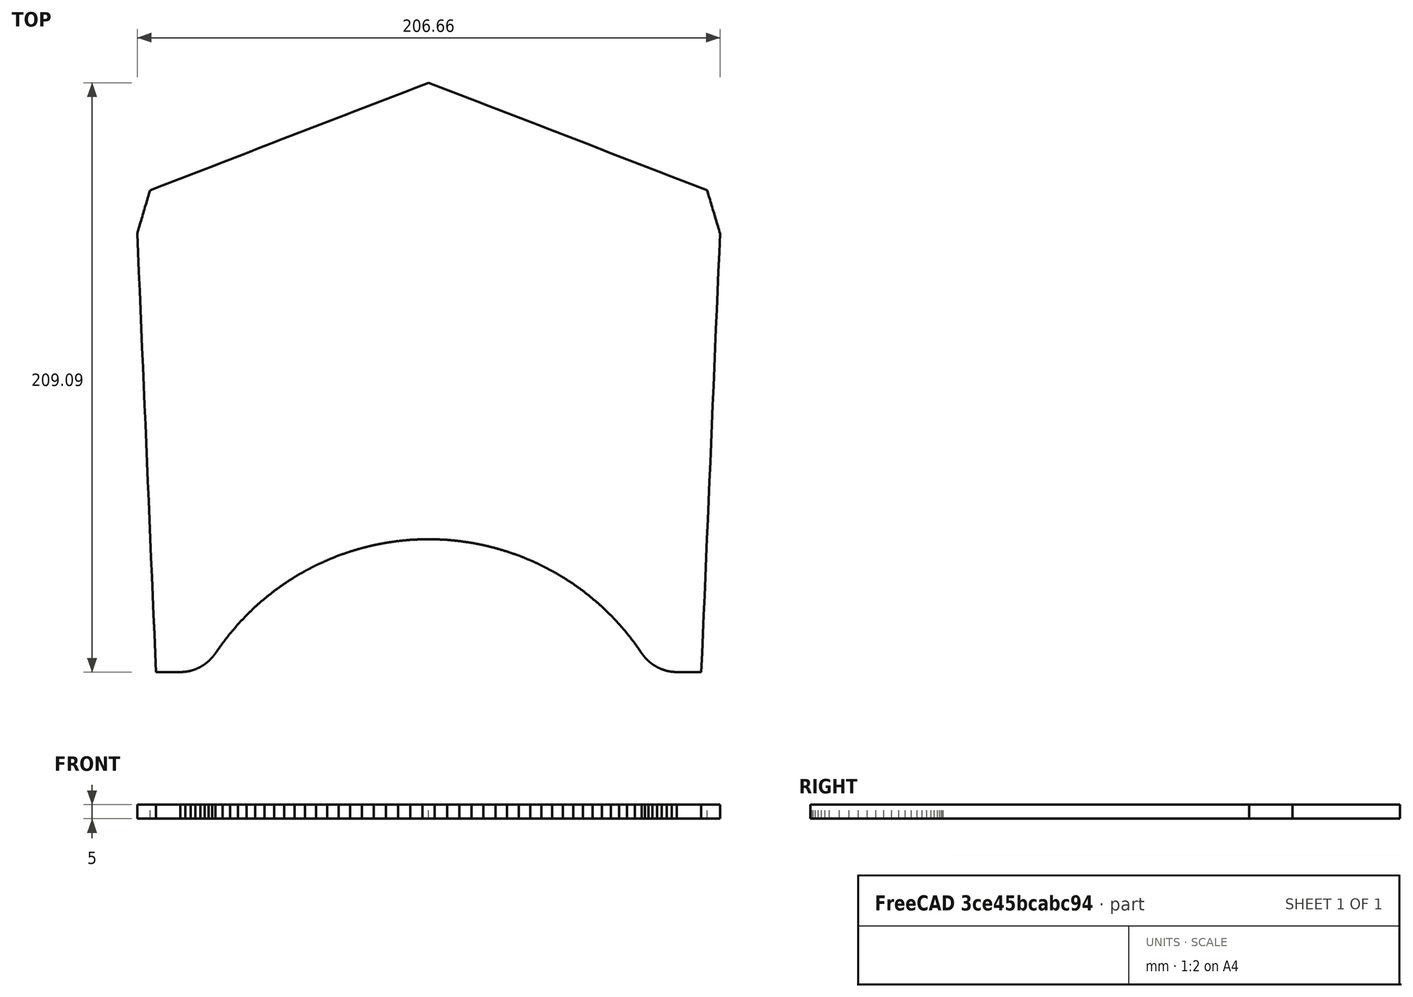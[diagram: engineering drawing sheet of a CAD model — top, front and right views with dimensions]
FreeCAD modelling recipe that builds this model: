
FCSTD DOCUMENT  (FreeCAD 0.19R)
Label: F-35_v2_parts_18
License: All rights reserved
LicenseURL: http://en.wikipedia.org/wiki/All_rights_reserved
objects: App::DocumentObjectGroup×2, PartDesign::CoordinateSystem×2, App::FeaturePython×1, Sketcher::SketchObject×1, PartDesign::Pad×1, PartDesign::Body×1, App::Part×1
note: 6 computed .brp shape members not serialized (recipe doc carries the construction recipe); baked Part::Feature solids carry a one-line shape summary decoded from their .brp

FEATURE [App::DocumentObjectGroup] Parts
FEATURE [PartDesign::CoordinateSystem] LCS_Origin
  AttacherType = Attacher::AttachEngine3D
  MapMode = 2
  Support = -> [X_Axis]
FEATURE [App::DocumentObjectGroup] Constraints
FEATURE [App::FeaturePython] Variables  # WARN: FeaturePython — macro-defined, semantics opaque (R4)
FEATURE [Sketcher::SketchObject] Sketch005
  FullyConstrained = false
  sketch-geometry (65):
    g0: BSplineCurve PolesCount=2 KnotsCount=2 Degree=1 IsPeriodic=0
    g1: BSplineCurve PolesCount=2 KnotsCount=2 Degree=1 IsPeriodic=0
    g2: BSplineCurve PolesCount=2 KnotsCount=2 Degree=1 IsPeriodic=0
    g3: BSplineCurve PolesCount=2 KnotsCount=2 Degree=1 IsPeriodic=0
    g4: BSplineCurve PolesCount=2 KnotsCount=2 Degree=1 IsPeriodic=0
    g5: BSplineCurve PolesCount=2 KnotsCount=2 Degree=1 IsPeriodic=0
    g6: BSplineCurve PolesCount=2 KnotsCount=2 Degree=1 IsPeriodic=0
    g7: BSplineCurve PolesCount=2 KnotsCount=2 Degree=1 IsPeriodic=0
    g8: BSplineCurve PolesCount=2 KnotsCount=2 Degree=1 IsPeriodic=0
    g9: BSplineCurve PolesCount=2 KnotsCount=2 Degree=1 IsPeriodic=0
    g10: BSplineCurve PolesCount=2 KnotsCount=2 Degree=1 IsPeriodic=0
    g11: BSplineCurve PolesCount=2 KnotsCount=2 Degree=1 IsPeriodic=0
    g12: BSplineCurve PolesCount=2 KnotsCount=2 Degree=1 IsPeriodic=0
    g13: BSplineCurve PolesCount=2 KnotsCount=2 Degree=1 IsPeriodic=0
    g14: BSplineCurve PolesCount=2 KnotsCount=2 Degree=1 IsPeriodic=0
    g15: BSplineCurve PolesCount=2 KnotsCount=2 Degree=1 IsPeriodic=0
    g16: BSplineCurve PolesCount=2 KnotsCount=2 Degree=1 IsPeriodic=0
    g17: BSplineCurve PolesCount=2 KnotsCount=2 Degree=1 IsPeriodic=0
    g18: BSplineCurve PolesCount=2 KnotsCount=2 Degree=1 IsPeriodic=0
    g19: BSplineCurve PolesCount=2 KnotsCount=2 Degree=1 IsPeriodic=0
    g20: BSplineCurve PolesCount=2 KnotsCount=2 Degree=1 IsPeriodic=0
    g21: BSplineCurve PolesCount=2 KnotsCount=2 Degree=1 IsPeriodic=0
    g22: BSplineCurve PolesCount=2 KnotsCount=2 Degree=1 IsPeriodic=0
    g23: BSplineCurve PolesCount=2 KnotsCount=2 Degree=1 IsPeriodic=0
    g24: BSplineCurve PolesCount=2 KnotsCount=2 Degree=1 IsPeriodic=0
    g25: BSplineCurve PolesCount=2 KnotsCount=2 Degree=1 IsPeriodic=0
    g26: BSplineCurve PolesCount=2 KnotsCount=2 Degree=1 IsPeriodic=0
    g27: BSplineCurve PolesCount=2 KnotsCount=2 Degree=1 IsPeriodic=0
    g28: BSplineCurve PolesCount=2 KnotsCount=2 Degree=1 IsPeriodic=0
    g29: BSplineCurve PolesCount=2 KnotsCount=2 Degree=1 IsPeriodic=0
    g30: BSplineCurve PolesCount=2 KnotsCount=2 Degree=1 IsPeriodic=0
    g31: BSplineCurve PolesCount=2 KnotsCount=2 Degree=1 IsPeriodic=0
    g32: BSplineCurve PolesCount=2 KnotsCount=2 Degree=1 IsPeriodic=0
    g33: BSplineCurve PolesCount=2 KnotsCount=2 Degree=1 IsPeriodic=0
    g34: BSplineCurve PolesCount=2 KnotsCount=2 Degree=1 IsPeriodic=0
    g35: BSplineCurve PolesCount=2 KnotsCount=2 Degree=1 IsPeriodic=0
    g36: BSplineCurve PolesCount=2 KnotsCount=2 Degree=1 IsPeriodic=0
    g37: BSplineCurve PolesCount=2 KnotsCount=2 Degree=1 IsPeriodic=0
    g38: BSplineCurve PolesCount=2 KnotsCount=2 Degree=1 IsPeriodic=0
    g39: BSplineCurve PolesCount=2 KnotsCount=2 Degree=1 IsPeriodic=0
    g40: BSplineCurve PolesCount=2 KnotsCount=2 Degree=1 IsPeriodic=0
    g41: BSplineCurve PolesCount=2 KnotsCount=2 Degree=1 IsPeriodic=0
    g42: BSplineCurve PolesCount=2 KnotsCount=2 Degree=1 IsPeriodic=0
    g43: BSplineCurve PolesCount=2 KnotsCount=2 Degree=1 IsPeriodic=0
    g44: BSplineCurve PolesCount=2 KnotsCount=2 Degree=1 IsPeriodic=0
    g45: BSplineCurve PolesCount=2 KnotsCount=2 Degree=1 IsPeriodic=0
    g46: BSplineCurve PolesCount=2 KnotsCount=2 Degree=1 IsPeriodic=0
    g47: BSplineCurve PolesCount=2 KnotsCount=2 Degree=1 IsPeriodic=0
    g48: BSplineCurve PolesCount=2 KnotsCount=2 Degree=1 IsPeriodic=0
    g49: BSplineCurve PolesCount=2 KnotsCount=2 Degree=1 IsPeriodic=0
    g50: BSplineCurve PolesCount=2 KnotsCount=2 Degree=1 IsPeriodic=0
    g51: BSplineCurve PolesCount=2 KnotsCount=2 Degree=1 IsPeriodic=0
    g52: BSplineCurve PolesCount=2 KnotsCount=2 Degree=1 IsPeriodic=0
    g53: BSplineCurve PolesCount=2 KnotsCount=2 Degree=1 IsPeriodic=0
    g54: BSplineCurve PolesCount=2 KnotsCount=2 Degree=1 IsPeriodic=0
    g55: BSplineCurve PolesCount=2 KnotsCount=2 Degree=1 IsPeriodic=0
    g56: BSplineCurve PolesCount=2 KnotsCount=2 Degree=1 IsPeriodic=0
    g57: BSplineCurve PolesCount=2 KnotsCount=2 Degree=1 IsPeriodic=0
    g58: BSplineCurve PolesCount=2 KnotsCount=2 Degree=1 IsPeriodic=0
    g59: BSplineCurve PolesCount=2 KnotsCount=2 Degree=1 IsPeriodic=0
    g60: BSplineCurve PolesCount=2 KnotsCount=2 Degree=1 IsPeriodic=0
    g61: BSplineCurve PolesCount=2 KnotsCount=2 Degree=1 IsPeriodic=0
    g62: BSplineCurve PolesCount=2 KnotsCount=2 Degree=1 IsPeriodic=0
    g63: BSplineCurve PolesCount=2 KnotsCount=2 Degree=1 IsPeriodic=0
    g64: BSplineCurve PolesCount=2 KnotsCount=2 Degree=1 IsPeriodic=0
  constraints (54):
    c: Coincident(g0,g1)
    c: Coincident(g1,g2)
    c: Coincident(g2,g3)
    c: Coincident(g3,g4)
    c: Coincident(g4,g5)
    c: Coincident(g5,g6)
    c: Coincident(g6,g7)
    c: Coincident(g9,g10)
    c: Coincident(g10,g11)
    c: Coincident(g11,g12)
    c: Coincident(g12,g13)
    c: Coincident(g13,g14)
    c: Coincident(g14,g15)
    c: Coincident(g15,g16)
    c: Coincident(g16,g17)
    c: Coincident(g17,g18)
    c: Coincident(g18,g19)
    c: Coincident(g19,g20)
    c: Coincident(g20,g21)
    c: Coincident(g21,g22)
    c: Coincident(g22,g23)
    c: Coincident(g23,g24)
    c: Coincident(g24,g25)
    c: Coincident(g25,g26)
    c: Coincident(g26,g27)
    c: Coincident(g27,g28)
    c: Coincident(g28,g29)
    c: Coincident(g29,g30)
    c: Coincident(g30,g31)
    c: Coincident(g31,g32)
    c: Coincident(g32,g33)
    c: Coincident(g33,g34)
    c: Coincident(g34,g35)
    c: Coincident(g35,g36)
    c: Coincident(g36,g37)
    c: Coincident(g37,g38)
    c: Coincident(g38,g39)
    c: Coincident(g39,g40)
    c: Coincident(g40,g41)
    c: Coincident(g41,g42)
    c: Coincident(g42,g43)
    c: Coincident(g43,g44)
    c: Coincident(g44,g45)
    c: Coincident(g45,g46)
    c: Coincident(g46,g47)
    c: Coincident(g47,g48)
    c: Coincident(g48,g49)
    c: Coincident(g51,g52)
    c: Coincident(g52,g53)
    c: Coincident(g53,g54)
    c: Coincident(g54,g55)
    c: Coincident(g55,g56)
    c: Coincident(g56,g57)
    c: Coincident(g57,g58)
FEATURE [PartDesign::Pad] Pad001
  Direction = (1,1,1)
  Length = 5
  Length2 = 100
  Profile = -> Sketch005
  Type = 0
FEATURE [PartDesign::Body] Body005  label="Part18"
  Group = -> [Sketch005,Pad001]
  Origin = -> Origin006
  Tip = -> Pad001
FEATURE [PartDesign::CoordinateSystem] LCS_1
  AttacherType = Attacher::AttachEngine3D
  AttachmentOffset = pos=(0,0,-155.712) rot=(0,0,1;0rad)
  MapMode = 7
  Placement = pos=(114.358,-454.859,-2.59e-14) rot=(0.999542,0.021409,0.021409;1.57126rad)
  Support = -> [Pad001]
FEATURE [App::Part] Model
  Configuration = 0
  Group = -> [LCS_Origin,Constraints,Variables,Body005,LCS_1]
  Origin = -> Origin
  Type = Assembly4 Model
